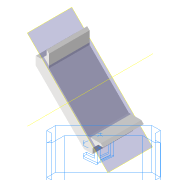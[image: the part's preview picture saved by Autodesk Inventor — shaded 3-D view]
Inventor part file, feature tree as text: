
AUTODESK INVENTOR PART (.ipt)
format: ipt  version: 2022 (Build 260153000, 153)  size: 277,504 bytes
history: native  units: mm
features: reference x7, sketch x5, other x4, extrude x3, plane x3, projected_geometry x3, emboss x2
ambient origin geometry x8: Origin, YZ Plane, XZ Plane, XY Plane, X Axis, Y Axis, Z Axis, Center Point
bodies: Solid1 (feature_tree)
feature tree (27):
  extrude  "Extrusion1"  Depth=30.0mm
  plane  "Work Plane1"
  extrude  "Extrusion7"  Depth=1.0mm TaperAngle=0.0deg
  emboss  "Emboss1"
  emboss  "Emboss2"
  extrude  "Extrusion9"  Depth=1.0mm TaperAngle=0.0deg
  plane  "Arbeitsebene4"
  plane  "Arbeitsebene5"
  sketch  "Sketch1"  dims[d3=30.0mm d4=0.0mm d28=41.0mm]
  sketch  "Sketch7"  dims[d29=1.0mm d30=10.0mm d31=0.0mm]
  projected_geometry  "Projected Loop3"
  sketch  "Sketch10"  dims[d40=1.5mm d41=1.5mm d42=1.5mm d43=10.0mm d44=10.0mm d45=1.0mm d46=0.0mm]
  sketch  "Sketch11"  dims[d47=120.0deg d48=1.5mm d49=1.5mm d50=1.5mm d51=1.5mm]
  projected_geometry  "Projected Loop6"
  sketch  "Sketch12"  dims[d52=1.5mm d53=0.0mm d54=60.0deg d55=1.5mm d57=120.0deg d58=1.5mm d59=120.0deg d60=1.5mm d63=2.0mm d64=0.0mm d74=0.0mm d75=8.267949mm d76=120.0deg d77=8.267949mm d78=4.160254mm d79=5.660254mm d80=120.0deg d81=120.0deg d82=3.0mm d83=3.0mm d84=3.0mm d85=1.5mm d86=7.160254mm d87=7.160254mm d88=4.160254mm d89=1.732051mm d90=5.660254mm d91=1.732051mm d92=4.160254mm d96=0.1mm d97=0.0mm d99=0.0mm d101=0.1mm d102=0.1mm d103=0.1mm]
  projected_geometry  "Projected Loop7"
  reference  "Referenz12"
  reference  "Referenz13"
  reference  "Referenz14"
  reference  "Referenz15"
  reference  "Referenz16"
  reference  "Referenz17"
  reference  "Referenz18"
  other  "Assembly_Cube_Kinematic_Mirrormount_30x30_45_v3.iam"
  other  "Assembly_Cube_empty_IM_v3:1"
  other  "10_Cube_1x1_IM:1"
  other  "10_Cube_1x1_IM:2"
